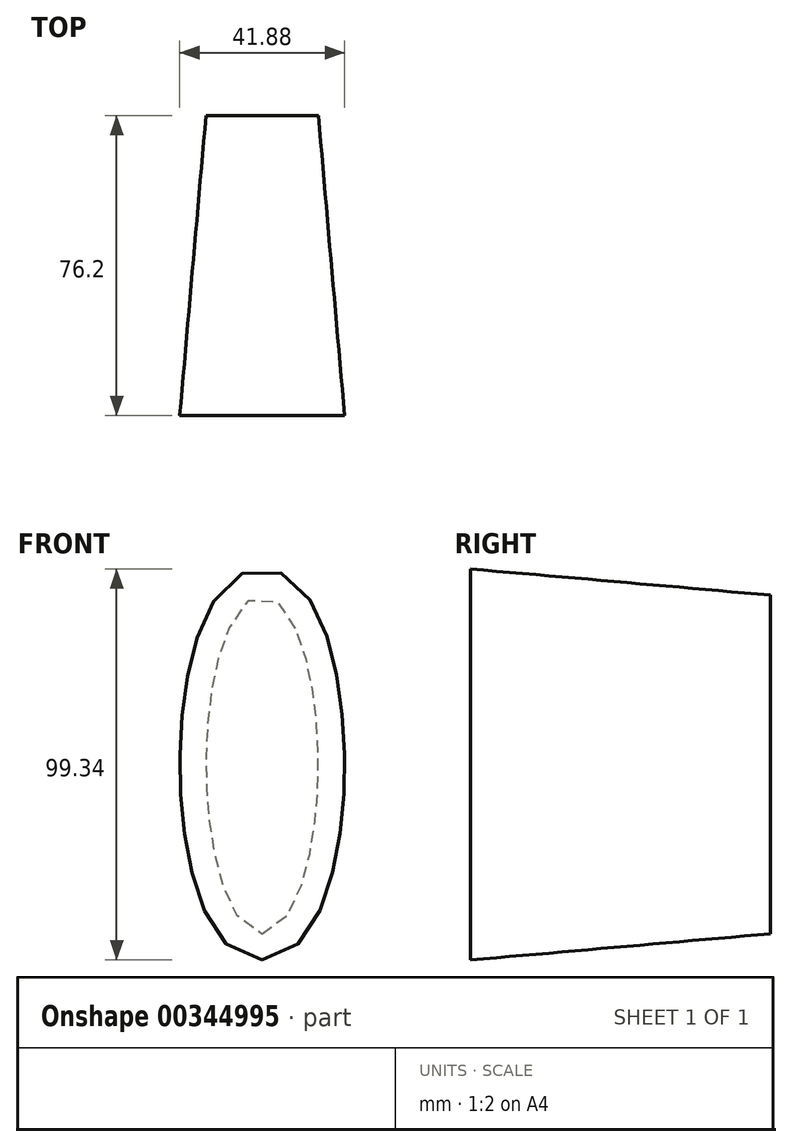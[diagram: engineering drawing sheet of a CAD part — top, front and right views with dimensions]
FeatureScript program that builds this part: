
annotation { "Feature Type Name" : "Feature", "Feature Type Description" : "" }
export const myFeature = defineFeature(function(context is Context, id is Id, definition is map)
    precondition{}
    {
        {
            var Q0;
            Q0=qCreatedBy(makeId("Front.planeOp"),FACE);
            var sketch = newSketch(context, id + "F0", { "sketchPlane" : qUnion([Q0])});
            skEllipse(sketch, "E0", {"center": v(0, 0) * mm, "majorRadius": 43 * mm, "minorRadius": 14.28 * mm, "majorAxis": v(0, 1)});
            skSolve(sketch);
        }
        {
            var Q0;
            Q0 = qSketchRegion(id + "F0", true);
            extrude(context, id + "F1", {"entities" : qUnion([Q0]), "depth" : 76.2 * mm, "hasDraft" : true, "draftAngle" : 5 * degree});
        }
        {
            var Q0;
            Q0=makeQuery(id+"F1.opExtrude","SWEPT_BODY",BODY,{"disambiguationData":[OSD([sQuery(id+"F0.wireOp",EDGE,"E0")])]});
            transform(context, id + "F2", {"entities" : qUnion([Q0]), "transformType" : TransformType.TRANSLATION_3D, "dx" : 0 * mm, "dy" : 38.1 * mm, "dz" : 0 * mm, "makeCopy" : false});
        }
    });
